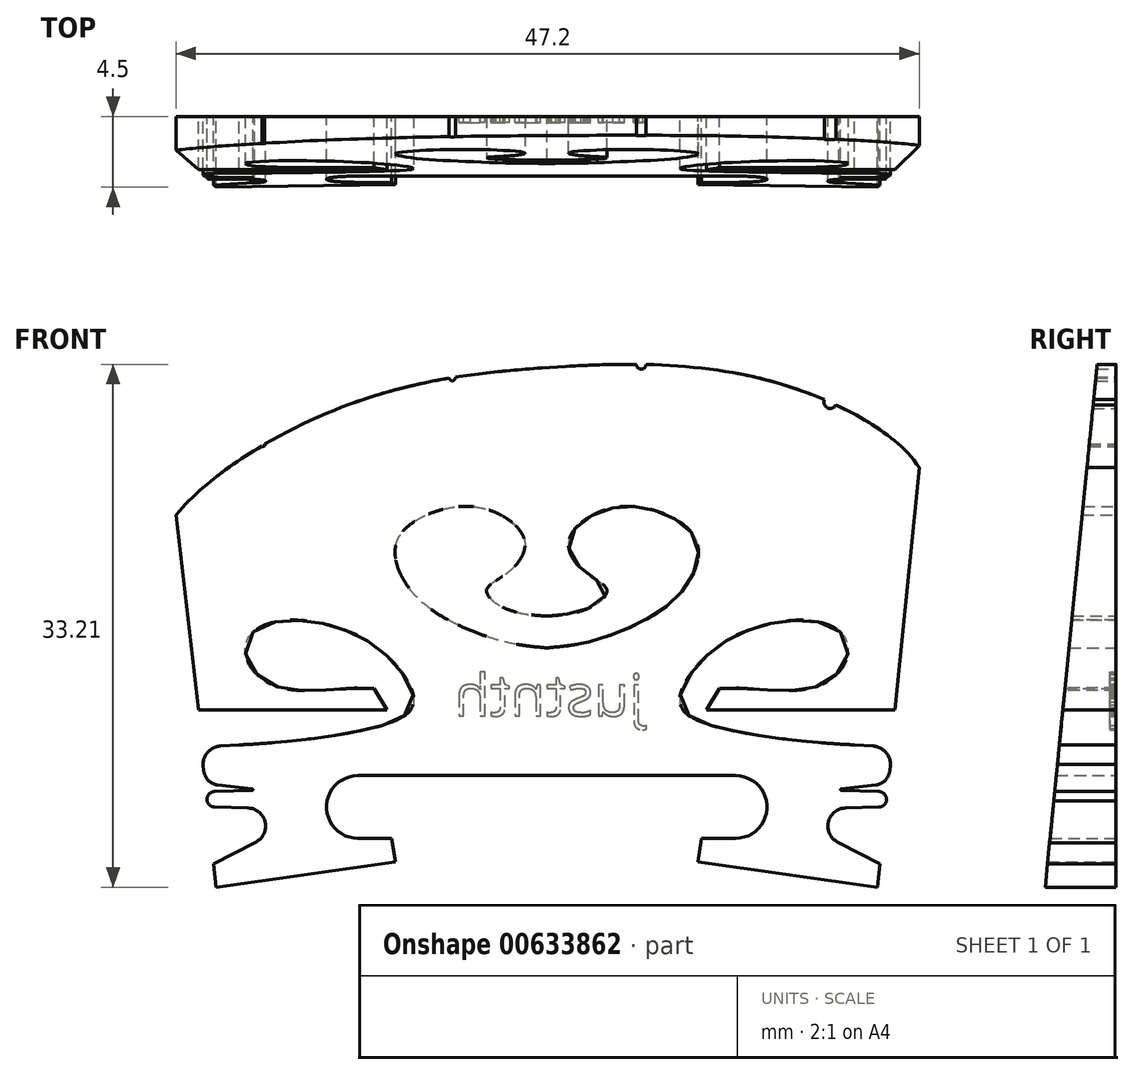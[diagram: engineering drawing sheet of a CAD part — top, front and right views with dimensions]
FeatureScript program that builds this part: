
annotation { "Feature Type Name" : "Feature", "Feature Type Description" : "" }
export const myFeature = defineFeature(function(context is Context, id is Id, definition is map)
    precondition{}
    {
        {
            var Q0;
            Q0=qCreatedBy(makeId("Front.planeOp"),FACE);
            var sketch = newSketch(context, id + "F0", { "sketchPlane" : qUnion([Q0])});
            skFitSpline(sketch, "E0", {"points": [v(-23.54, 23.66) * mm, v(-12.1, 30.83) * mm, v(0, 33) * mm, v(13.95, 32.22) * mm, v(23.66, 26.65) * mm], "startDerivative": vector(29.69, 35.16) * mm, "endDerivative": vector(19.16, -29.67) * mm});
            skLineSegment(sketch, "E1", {"start": v(21, 0) * mm, "end": v(9.61, 1.6) * mm});
            skLineSegment(sketch, "E2", {"start": v(9.61, 1.6) * mm, "end": v(9.82, 3.09) * mm});
            skLineSegment(sketch, "E3", {"start": v(9.82, 3.09) * mm, "end": v(12, 3.1) * mm});
            skLineSegment(sketch, "E4", {"start": v(12, 7.1) * mm, "end": v(0, 7.1) * mm});
            skPoint(sketch, "E5.visualSharp", {"position": v(1153.06, 7.1) * mm});
            skArc(sketch, "E5.filletArc", {"start": v(12, 3.1) * mm, "mid": v(14, 5.1) * mm, "end": v(12, 7.1) * mm});
            skLineSegment(sketch, "E6", {"start": v(21, 0) * mm, "end": v(21.16, 1.5) * mm});
            skPoint(sketch, "E7.visualSharp", {"position": v(11.23, 5.08) * mm});
            skFitSpline(sketch, "E8", {"points": [v(0, 15.2) * mm, v(4, 15.99) * mm, v(8.17, 18.33) * mm, v(9.57, 21.81) * mm, v(7.19, 23.82) * mm, v(3.6, 23.93) * mm, v(1.4, 21.97) * mm, v(2.5, 19.96) * mm, v(3.82, 18.86) * mm, v(2.74, 17.76) * mm, v(0, 17.22) * mm], "startDerivative": vector(53.54, 4.7) * mm, "endDerivative": vector(-27.32, -1.62) * mm});
            skFitSpline(sketch, "E9.MirrorCS", {"points": [v(0, 15.2) * mm, v(-4, 15.99) * mm, v(-8.17, 18.33) * mm, v(-9.57, 21.81) * mm, v(-7.19, 23.82) * mm, v(-3.6, 23.93) * mm, v(-1.4, 21.97) * mm, v(-2.5, 19.96) * mm, v(-3.82, 18.86) * mm, v(-2.74, 17.76) * mm, v(0, 17.22) * mm], "startDerivative": vector(-53.54, 4.7) * mm, "endDerivative": vector(27.32, -1.62) * mm});
            skLineSegment(sketch, "E10.MirrorCS", {"start": v(-12, 7.1) * mm, "end": v(0, 7.1) * mm});
            skArc(sketch, "E11.MirrorCS", {"start": v(-12.01, 3.1) * mm, "mid": v(-14, 5.1) * mm, "end": v(-12, 7.1) * mm});
            skLineSegment(sketch, "E12.MirrorCS", {"start": v(-9.85, 3.08) * mm, "end": v(-12.01, 3.1) * mm});
            skLineSegment(sketch, "E13.MirrorCS", {"start": v(-9.61, 1.6) * mm, "end": v(-9.85, 3.08) * mm});
            skLineSegment(sketch, "E14", {"start": v(-21.16, 1.5) * mm, "end": v(-21, 0) * mm});
            skFitSpline(sketch, "E15.MirrorCS", {"points": [v(10.96, 12.63) * mm, v(17.29, 12.8) * mm, v(19.14, 15.37) * mm, v(17, 16.9) * mm, v(12.21, 16.08) * mm, v(9.91, 14.46) * mm, v(8.57, 12.54) * mm, v(9.18, 10.8) * mm, v(19.55, 9.04) * mm], "startDerivative": vector(28.37, 3.52) * mm, "endDerivative": vector(23.7, -0.72) * mm});
            skLineSegment(sketch, "E16.MirrorCS", {"start": v(10.96, 12.63) * mm, "end": v(10.14, 11.25) * mm});
            skLineSegment(sketch, "E17", {"start": v(-18, 62.47) * mm, "end": v(-18, 22.93) * mm, "construction": true});
            skLineSegment(sketch, "E18", {"start": v(6, 60.56) * mm, "end": v(6, 29.37) * mm, "construction": true});
            skLineSegment(sketch, "E19", {"start": v(18, 61.03) * mm, "end": v(18, 25.82) * mm, "construction": true});
            skLineSegment(sketch, "E20", {"start": v(-6, 62.47) * mm, "end": v(-6, 28.49) * mm, "construction": true});
            skCircle(sketch, "E21", {"center": v(-18, 28.08) * mm, "radius": 0.1 * mm});
            skCircle(sketch, "E22", {"center": v(-6, 32.36) * mm, "radius": 0.2 * mm});
            skCircle(sketch, "E23", {"center": v(18, 30.8) * mm, "radius": 0.4 * mm});
            skCircle(sketch, "E24", {"center": v(6, 33.2) * mm, "radius": 0.3 * mm});
            skLineSegment(sketch, "E25", {"start": v(23.66, 26.65) * mm, "end": v(22.12, 11.25) * mm});
            skLineSegment(sketch, "E26", {"start": v(-21, 0) * mm, "end": v(-9.61, 1.6) * mm});
            skLineSegment(sketch, "E27", {"start": v(22.12, 11.25) * mm, "end": v(10.14, 11.25) * mm});
            skLineSegment(sketch, "E28", {"start": v(21.16, 1.5) * mm, "end": v(18.56, 2.82) * mm});
            skLineSegment(sketch, "E29", {"start": v(20.7, 8.97) * mm, "end": v(19.55, 9.04) * mm});
            skLineSegment(sketch, "E30", {"start": v(18.96, 5.03) * mm, "end": v(21.1, 5.08) * mm});
            skArc(sketch, "E31", {"start": v(18.96, 5.03) * mm, "mid": v(17.86, 4.1) * mm, "end": v(18.56, 2.82) * mm});
            skPoint(sketch, "E32.visualSharp", {"position": v(21.52, 5.1) * mm});
            skArc(sketch, "E32.filletArc", {"start": v(21.1, 5.08) * mm, "mid": v(21.4, 5.2) * mm, "end": v(21.57, 5.47) * mm});
            skLineSegment(sketch, "E33", {"start": v(21.57, 5.47) * mm, "end": v(21.58, 5.52) * mm});
            skArc(sketch, "E34.filletArc", {"start": v(21.58, 5.52) * mm, "mid": v(21.45, 5.9) * mm, "end": v(21.08, 6.07) * mm});
            skArc(sketch, "E35.filletArc", {"start": v(21.83, 7.8) * mm, "mid": v(21.5, 8.6) * mm, "end": v(20.7, 8.97) * mm});
            skLineSegment(sketch, "E36", {"start": v(21.08, 6.07) * mm, "end": v(18.71, 6.15) * mm});
            skFitSpline(sketch, "E37.MirrorCS", {"points": [v(-10.96, 12.63) * mm, v(-17.29, 12.8) * mm, v(-19.14, 15.37) * mm, v(-17, 16.9) * mm, v(-12.21, 16.08) * mm, v(-9.91, 14.46) * mm, v(-8.57, 12.54) * mm, v(-9.18, 10.8) * mm, v(-19.55, 9.04) * mm], "startDerivative": vector(-28.37, 3.52) * mm, "endDerivative": vector(-23.7, -0.72) * mm});
            skLineSegment(sketch, "E38.MirrorCS", {"start": v(-10.96, 12.63) * mm, "end": v(-10.14, 11.25) * mm});
            skLineSegment(sketch, "E39.MirrorCS", {"start": v(-22.12, 11.25) * mm, "end": v(-10.14, 11.25) * mm});
            skLineSegment(sketch, "E40.MirrorCS", {"start": v(-18.96, 5.03) * mm, "end": v(-21.1, 5.08) * mm});
            skArc(sketch, "E41.MirrorCS", {"start": v(-18.96, 5.03) * mm, "mid": v(-17.86, 4.1) * mm, "end": v(-18.56, 2.82) * mm});
            skLineSegment(sketch, "E42.MirrorCS", {"start": v(-21.16, 1.5) * mm, "end": v(-18.56, 2.82) * mm});
            skLineSegment(sketch, "E43", {"start": v(-22.12, 11.25) * mm, "end": v(-23.54, 23.66) * mm});
            skLineSegment(sketch, "E44", {"start": v(18.7, 6.25) * mm, "end": v(20.9, 6.49) * mm});
            skLineSegment(sketch, "E45", {"start": v(21.78, 7.37) * mm, "end": v(21.83, 7.8) * mm});
            skArc(sketch, "E46.filletArc", {"start": v(20.9, 6.49) * mm, "mid": v(21.5, 6.77) * mm, "end": v(21.78, 7.37) * mm});
            skPoint(sketch, "E47.visualSharp", {"position": v(18, 6.17) * mm});
            skArc(sketch, "E47.filletArc", {"start": v(18.7, 6.25) * mm, "mid": v(18.66, 6.2) * mm, "end": v(18.71, 6.15) * mm});
            skLineSegment(sketch, "E48.MirrorCS", {"start": v(-20.7, 8.97) * mm, "end": v(-19.55, 9.04) * mm});
            skArc(sketch, "E49.MirrorCS", {"start": v(-21.83, 7.8) * mm, "mid": v(-21.5, 8.6) * mm, "end": v(-20.7, 8.97) * mm});
            skLineSegment(sketch, "E50.MirrorCS", {"start": v(-21.78, 7.37) * mm, "end": v(-21.83, 7.8) * mm});
            skArc(sketch, "E51.MirrorCS", {"start": v(-20.9, 6.49) * mm, "mid": v(-21.5, 6.77) * mm, "end": v(-21.78, 7.37) * mm});
            skLineSegment(sketch, "E52.MirrorCS", {"start": v(-18.7, 6.25) * mm, "end": v(-20.9, 6.49) * mm});
            skArc(sketch, "E53.MirrorCS", {"start": v(-18.7, 6.25) * mm, "mid": v(-18.66, 6.2) * mm, "end": v(-18.71, 6.15) * mm});
            skLineSegment(sketch, "E54.MirrorCS", {"start": v(-21.08, 6.07) * mm, "end": v(-18.71, 6.15) * mm});
            skArc(sketch, "E55.MirrorCS", {"start": v(-21.58, 5.52) * mm, "mid": v(-21.45, 5.9) * mm, "end": v(-21.08, 6.07) * mm});
            skArc(sketch, "E56.MirrorCS", {"start": v(-21.1, 5.08) * mm, "mid": v(-21.4, 5.2) * mm, "end": v(-21.57, 5.47) * mm});
            skLineSegment(sketch, "E57.MirrorCS", {"start": v(-21.57, 5.47) * mm, "end": v(-21.58, 5.52) * mm});
            skSolve(sketch);
        }
        {
            var Q0;
            {var subQ1=sQuery(id+"F0.wireOp",EDGE,"E0");Q0=makeQuery(id+"F0.imprint","IMPRINT",FACE,{"disambiguationData":[TD([[makeQuery(id+"F0.imprint","IMPRINT",EDGE,{"derivedFrom":subQ1}),-1.0]])]});}
            extrude(context, id + "F1", {"entities" : qUnion([Q0]), "depth" : 4.5 * mm, "offsetDistance" : 25.4 * mm});
        }
        {
            var Q0;
            Q0=qCreatedBy(makeId("Right.planeOp"),FACE);
            var sketch = newSketch(context, id + "F2", { "sketchPlane" : qUnion([Q0])});
            skLineSegment(sketch, "E58", {"start": v(-1.2, 78.1) * mm, "end": v(-1.2, 1.9) * mm});
            skLineSegment(sketch, "E59", {"start": v(12.46, 33.21) * mm, "end": v(-25.03, 33.21) * mm});
            skLineSegment(sketch, "E60", {"start": v(-4.5, -2.46) * mm, "end": v(-4.5, 45.63) * mm});
            skLineSegment(sketch, "E61", {"start": v(-1.2, 33.21) * mm, "end": v(-4.5, 0) * mm});
            skLineSegment(sketch, "E62", {"start": v(-4.5, 0) * mm, "end": v(-9, 0) * mm});
            skLineSegment(sketch, "E63", {"start": v(-9, 0) * mm, "end": v(-7.85, 33.21) * mm});
            skLineSegment(sketch, "E64", {"start": v(-7.85, 33.21) * mm, "end": v(-1.2, 33.21) * mm});
            skLineSegment(sketch, "E65.top", {"start": v(-7.85, 40.77) * mm, "end": v(-1.2, 40.77) * mm});
            skLineSegment(sketch, "E65.left", {"start": v(-7.85, 33.21) * mm, "end": v(-7.85, 40.77) * mm});
            skLineSegment(sketch, "E65.right", {"start": v(-1.2, 33.21) * mm, "end": v(-1.2, 40.77) * mm});
            skSolve(sketch);
        }
        {
            var Q0;
            {var subQ0=sQuery(id+"F2.wireOp",EDGE,"E62");Q0=makeQuery(id+"F2.imprint","IMPRINT",FACE,{"disambiguationData":[TD([[makeQuery(id+"F2.imprint","IMPRINT",EDGE,{"derivedFrom":subQ0}),-1.0]])]});}
            var Q1;
            {var subQ0=sQuery(id+"F2.wireOp",EDGE,"E61");Q1=makeQuery(id+"F2.imprint","IMPRINT",FACE,{"disambiguationData":[TD([[makeQuery(id+"F2.imprint","IMPRINT",EDGE,{"derivedFrom":subQ0}),-1.0]])]});}
            var Q2;
            {var subQ5=sQuery(id+"F2.wireOp",EDGE,"E65.left");Q2=makeQuery(id+"F2.imprint","IMPRINT",FACE,{"disambiguationData":[TD([[makeQuery(id+"F2.imprint","IMPRINT",EDGE,{"derivedFrom":subQ5}),-1.0]])]});}
            var Q3;
            {var subQ5=sQuery(id+"F2.wireOp",EDGE,"E65.right");Q3=makeQuery(id+"F2.imprint","IMPRINT",FACE,{"disambiguationData":[TD([[makeQuery(id+"F2.imprint","IMPRINT",EDGE,{"derivedFrom":subQ5}),1.0]])]});}
            extrude(context, id + "F3", {"entities" : qUnion([Q0, Q1, Q2, Q3]), "operationType" : NewBodyOperationType.REMOVE, "endBound" : BoundingType.SYMMETRIC, "depth" : 60 * mm, "offsetDistance" : 25.4 * mm});
        }
        {
            var Q0;
            Q0=makeQuery(id+"F1.opExtrude","CAP_FACE",FACE,{"disambiguationData":[OSD([sQuery(id+"F0.wireOp",EDGE,"E0"),sQuery(id+"F0.wireOp",EDGE,"E1"),sQuery(id+"F0.wireOp",EDGE,"E2"),sQuery(id+"F0.wireOp",EDGE,"E3"),sQuery(id+"F0.wireOp",EDGE,"E4"),sQuery(id+"F0.wireOp",EDGE,"E5.filletArc"),sQuery(id+"F0.wireOp",EDGE,"E6"),sQuery(id+"F0.wireOp",EDGE,"E8"),sQuery(id+"F0.wireOp",EDGE,"E9.MirrorCS"),sQuery(id+"F0.wireOp",EDGE,"E10.MirrorCS"),sQuery(id+"F0.wireOp",EDGE,"E11.MirrorCS"),sQuery(id+"F0.wireOp",EDGE,"E12.MirrorCS"),sQuery(id+"F0.wireOp",EDGE,"E13.MirrorCS"),sQuery(id+"F0.wireOp",EDGE,"99c2ba22-9a41-4c2a-bd8a-ffb563d2db590.MirrorCS"),sQuery(id+"F0.wireOp",EDGE,"E14"),sQuery(id+"F0.wireOp",EDGE,"sNap6CoO-IBVS-i1IY-ntVr-FjdyHk4U1fLk"),sQuery(id+"F0.wireOp",EDGE,"Q49nbHIn-tZww-OQF0-PmV4-upVZ2FfT46EY"),sQuery(id+"F0.wireOp",EDGE,"cacc4af9-22af-473b-8ac6-10344cc65f12.filletArc"),sQuery(id+"F0.wireOp",EDGE,"b2179551-9911-4662-ab98-ed61c98f1fae0.MirrorCS"),sQuery(id+"F0.wireOp",EDGE,"WLDu3wvJ-hjGy-TZ6D-QxCG-5IQINUcYNDWe"),sQuery(id+"F0.wireOp",EDGE,"c432bdc4-3a2f-4fb0-98df-54dfc78423e7.filletArc"),sQuery(id+"F0.wireOp",EDGE,"686801cf-beb7-4a0b-9bdc-b307e84039be.filletArc"),sQuery(id+"F0.wireOp",EDGE,"xwyop2li-xI9W-UFQn-VAwa-afb1EGiimQMJ"),sQuery(id+"F0.wireOp",EDGE,"5a9beed9-85af-4595-b0f8-0b7d7c26e17c"),sQuery(id+"F0.wireOp",EDGE,"bzGZhi7p-2t2n-dACa-pQoM-uhUXtXE2D66O"),sQuery(id+"F0.wireOp",EDGE,"yywPAmDP-Yir0-P9Cb-WB6Q-Zl7V1TjRpGde"),sQuery(id+"F0.wireOp",EDGE,"E15.MirrorCS"),sQuery(id+"F0.wireOp",EDGE,"E16.MirrorCS"),sQuery(id+"F0.wireOp",EDGE,"PqBrF7gv-Diou-TzOB-6hR5-WF0VOCTdd9Ml"),sQuery(id+"F0.wireOp",EDGE,"irIPY5CA-CWUD-HGs8-Lafv-b9PyqiYwdKW4"),sQuery(id+"F0.wireOp",EDGE,"N699qDvk-ju4z-pMcA-En7K-C2CTM2OkSit7"),sQuery(id+"F0.wireOp",EDGE,"uBNGByd7-gyzj-997R-8Wxi-t9WqYOMEbmyB"),sQuery(id+"F0.wireOp",EDGE,"5093e992-0bc9-46ed-b494-589bb84dc8b9.filletArc"),sQuery(id+"F0.wireOp",EDGE,"d6a4b0fc-a71b-4a5d-b080-7cea932b6cd3.filletArc"),sQuery(id+"F0.wireOp",EDGE,"E21"),sQuery(id+"F0.wireOp",EDGE,"E22"),sQuery(id+"F0.wireOp",EDGE,"E23"),sQuery(id+"F0.wireOp",EDGE,"E24"),sQuery(id+"F0.wireOp",EDGE,"zmxQx3sE-Abgh-AzOG-xcvg-COG9eKqwMoW1"),sQuery(id+"F0.wireOp",EDGE,"6rnEQyg1-XuVb-NNO3-yQ0c-2cqNmvtJoFj3"),sQuery(id+"F0.wireOp",EDGE,"a740fce4-74ea-4a46-8614-070f5a65ce19.filletArc"),sQuery(id+"F0.wireOp",EDGE,"47d1662d-1cdc-404f-a2f1-9a71518fff21.filletArc"),sQuery(id+"F0.wireOp",EDGE,"x81WzDIV-gmfL-YwrE-CoO7-FSQeT6FRB7PQ"),sQuery(id+"F0.wireOp",EDGE,"GdfCoyAb-hPPH-aXcI-0p9N-VLlFjwOMujNR"),sQuery(id+"F0.wireOp",EDGE,"af57f127-2944-47e9-8a9b-73b34502bf92.filletArc"),sQuery(id+"F0.wireOp",EDGE,"19e7adce-8ca8-4fdb-b1fc-b8dd92e8bc45.filletArc")])],"isStart":true});
            var sketch = newSketch(context, id + "F4", { "sketchPlane" : qUnion([Q0])});
            skText(sketch, "E66", { "text": "justnth", "fontName": "OpenSans-Regular.ttf"});
            const initialGuessF4  = {"E66": [-0.00615, 0.01088, 1, 0, 0.00264]};
            skSetInitialGuess(sketch, initialGuessF4);
            skSolve(sketch);
        }
        {
            var Q0;
            Q0 = qSketchRegion(id + "F4", true);
            extrude(context, id + "F5", {"entities" : qUnion([Q0]), "operationType" : NewBodyOperationType.REMOVE, "oppositeDirection" : true, "depth" : 0.4 * mm, "offsetDistance" : 25.4 * mm});
        }
    });
